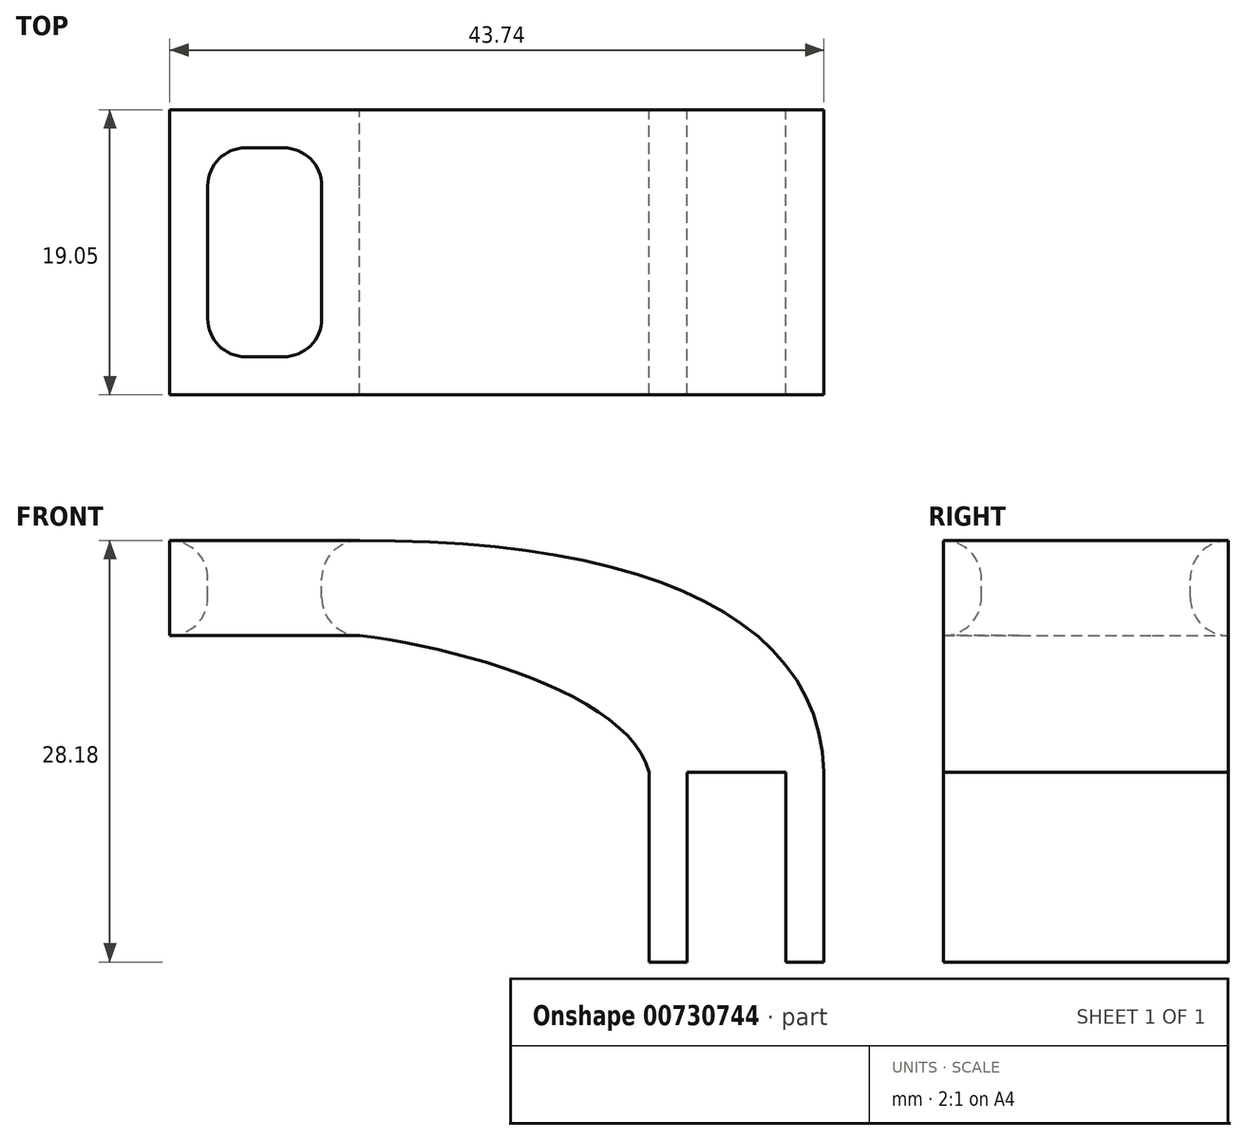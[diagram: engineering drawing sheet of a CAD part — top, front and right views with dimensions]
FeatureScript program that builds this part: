
annotation { "Feature Type Name" : "Feature", "Feature Type Description" : "" }
export const myFeature = defineFeature(function(context is Context, id is Id, definition is map)
    precondition{}
    {
        {
            var Q0;
            Q0=qCreatedBy(makeId("Front.planeOp"),FACE);
            var sketch = newSketch(context, id + "F0", { "sketchPlane" : qUnion([Q0])});
            skLineSegment(sketch, "E0.bottom", {"start": v(3.3, 6.35) * mm, "end": v(-3.3, 6.35) * mm});
            skLineSegment(sketch, "E0.left", {"start": v(3.3, 6.35) * mm, "end": v(3.3, -6.35) * mm});
            skLineSegment(sketch, "E0.right", {"start": v(-3.3, 6.35) * mm, "end": v(-3.3, -6.35) * mm});
            skPoint(sketch, "E0.middle", {"position": v(0, 0) * mm});
            skLineSegment(sketch, "E1.top", {"start": v(-3.3, -6.35) * mm, "end": v(-5.84, -6.35) * mm});
            skLineSegment(sketch, "E1.right", {"start": v(-5.84, 6.35) * mm, "end": v(-5.84, -6.35) * mm});
            skLineSegment(sketch, "E2.top", {"start": v(3.3, -6.35) * mm, "end": v(5.84, -6.35) * mm});
            skLineSegment(sketch, "E2.right", {"start": v(5.84, 6.35) * mm, "end": v(5.84, -6.35) * mm});
            skLineSegment(sketch, "E3.bottom", {"start": v(-25.2, 15.48) * mm, "end": v(-37.9, 15.48) * mm});
            skLineSegment(sketch, "E3.top", {"start": v(-25.2, 21.83) * mm, "end": v(-37.9, 21.83) * mm});
            skLineSegment(sketch, "E3.right", {"start": v(-37.9, 15.48) * mm, "end": v(-37.9, 21.83) * mm});
            skPoint(sketch, "E3.middle", {"position": v(-31.55, 18.65) * mm});
            skFitSpline(sketch, "E4", {"points": [v(-25.2, 21.83) * mm, v(5.84, 6.35) * mm], "startDerivative": vector(55.67, 0.15) * mm, "endDerivative": vector(0.93, -31.98) * mm});
            skFitSpline(sketch, "E5", {"points": [v(-25.2, 15.48) * mm, v(-5.84, 6.35) * mm], "startDerivative": vector(22.48, -2.8) * mm, "endDerivative": vector(3.82, -14.84) * mm});
            skSolve(sketch);
        }
        {
            var Q0;
            Q0=makeQuery(id+"F0.imprint","IMPRINT",FACE,{"disambiguationData":[TD([[makeQuery(id+"F0.imprint","IMPRINT",EDGE,{"derivedFrom":sQuery(id+"F0.wireOp",EDGE,"E0.bottom")}),-1.0]])]});
            extrude(context, id + "F1", {"entities" : qUnion([Q0]), "depth" : 19.05 * mm, "offsetDistance" : 25.4 * mm});
        }
        {
            var Q0;
            Q0=makeQuery(id+"F1.opExtrude","SWEPT_FACE",FACE,{"disambiguationData":[OSD([sQuery(id+"F0.wireOp",EDGE,"E3.top")])]});
            var sketch = newSketch(context, id + "F2", { "sketchPlane" : qUnion([Q0])});
            skLineSegment(sketch, "E6.0", {"start": v(-27.74, -2.54) * mm, "end": v(-35.36, -2.54) * mm});
            skLineSegment(sketch, "E6.1", {"start": v(-27.74, -16.51) * mm, "end": v(-27.74, -2.54) * mm});
            skLineSegment(sketch, "E6.2", {"start": v(-35.36, -16.51) * mm, "end": v(-27.74, -16.51) * mm});
            skLineSegment(sketch, "E6.3", {"start": v(-35.36, -2.54) * mm, "end": v(-35.36, -16.51) * mm});
            skSolve(sketch);
        }
        {
            var Q0;
            Q0=makeQuery(id+"F2.imprint","IMPRINT",FACE,{"disambiguationData":[TD([[makeQuery(id+"F2.imprint","IMPRINT",EDGE,{"derivedFrom":sQuery(id+"F2.wireOp",EDGE,"E6.0")}),1.0]])]});
            extrude(context, id + "F3", {"entities" : qUnion([Q0]), "operationType" : NewBodyOperationType.REMOVE, "oppositeDirection" : true, "depth" : 6.35 * mm, "offsetDistance" : 25.4 * mm});
        }
        {
            var Q0;
            Q0=makeQuery(id+"F3.boolean.opBoolean","COPY",EDGE,{"derivedFrom":makeQuery(id+"F3.opExtrude","SWEPT_EDGE",EDGE,{"disambiguationData":[OSD([sQuery(id+"F2.wireOp",EDGE,"E6.0"),sQuery(id+"F2.wireOp",EDGE,"E6.1")])]})});
            var Q1;
            Q1=makeQuery(id+"F3.boolean.opBoolean","COPY",EDGE,{"derivedFrom":makeQuery(id+"F3.opExtrude","SWEPT_EDGE",EDGE,{"disambiguationData":[OSD([sQuery(id+"F2.wireOp",EDGE,"E6.0"),sQuery(id+"F2.wireOp",EDGE,"E6.3")])]})});
            var Q2;
            Q2=makeQuery(id+"F3.boolean.opBoolean","COPY",EDGE,{"derivedFrom":makeQuery(id+"F3.opExtrude","SWEPT_EDGE",EDGE,{"disambiguationData":[OSD([sQuery(id+"F2.wireOp",EDGE,"E6.2"),sQuery(id+"F2.wireOp",EDGE,"E6.3")])]})});
            var Q3;
            Q3=makeQuery(id+"F3.boolean.opBoolean","COPY",EDGE,{"derivedFrom":makeQuery(id+"F3.opExtrude","SWEPT_EDGE",EDGE,{"disambiguationData":[OSD([sQuery(id+"F2.wireOp",EDGE,"E6.1"),sQuery(id+"F2.wireOp",EDGE,"E6.2")])]})});
            fillet(context, id + "F4", {"entities" : qUnion([Q0, Q1, Q2, Q3]), "radius" : 2.54 * mm, "tangentPropagation" : true, "allowEdgeOverflow" : false});
        }
        {
            var Q0;
            Q0=makeQuery(id+"F3.boolean.opBoolean","COPY",EDGE,{"derivedFrom":makeQuery(id+"F3.opExtrude","CAP_EDGE",EDGE,{"disambiguationData":[OSD([sQuery(id+"F2.wireOp",EDGE,"E6.3")])],"isStart":false})});
            var Q1;
            Q1=makeQuery(id+"F4.opFillet","BLEND_EDGE",EDGE,{"blendedFrom":[makeQuery(id+"F3.boolean.opBoolean","COPY",EDGE,{"derivedFrom":makeQuery(id+"F3.opExtrude","SWEPT_EDGE",EDGE,{"disambiguationData":[OSD([sQuery(id+"F2.wireOp",EDGE,"E6.2"),sQuery(id+"F2.wireOp",EDGE,"E6.3")])]})}),makeQuery(id+"F1.opExtrude","SWEPT_FACE",FACE,{"disambiguationData":[OSD([sQuery(id+"F0.wireOp",EDGE,"E3.bottom")])]})],"blendedInto":[makeQuery(id+"F1.opExtrude","SWEPT_FACE",FACE,{"disambiguationData":[OSD([sQuery(id+"F0.wireOp",EDGE,"E3.bottom")])]})]});
            var Q2;
            Q2=makeQuery(id+"F3.boolean.opBoolean","COPY",EDGE,{"derivedFrom":makeQuery(id+"F3.opExtrude","CAP_EDGE",EDGE,{"disambiguationData":[OSD([sQuery(id+"F2.wireOp",EDGE,"E6.2")])],"isStart":false})});
            var Q3;
            Q3=makeQuery(id+"F4.opFillet","BLEND_EDGE",EDGE,{"blendedFrom":[makeQuery(id+"F3.boolean.opBoolean","COPY",EDGE,{"derivedFrom":makeQuery(id+"F3.opExtrude","SWEPT_EDGE",EDGE,{"disambiguationData":[OSD([sQuery(id+"F2.wireOp",EDGE,"E6.1"),sQuery(id+"F2.wireOp",EDGE,"E6.2")])]})}),makeQuery(id+"F1.opExtrude","SWEPT_FACE",FACE,{"disambiguationData":[OSD([sQuery(id+"F0.wireOp",EDGE,"E3.bottom")])]})],"blendedInto":[makeQuery(id+"F1.opExtrude","SWEPT_FACE",FACE,{"disambiguationData":[OSD([sQuery(id+"F0.wireOp",EDGE,"E3.bottom")])]})]});
            var Q4;
            Q4=makeQuery(id+"F3.boolean.opBoolean","COPY",EDGE,{"derivedFrom":makeQuery(id+"F3.opExtrude","CAP_EDGE",EDGE,{"disambiguationData":[OSD([sQuery(id+"F2.wireOp",EDGE,"E6.1")])],"isStart":false})});
            var Q5;
            Q5=makeQuery(id+"F3.boolean.opBoolean","COPY",EDGE,{"derivedFrom":makeQuery(id+"F3.opExtrude","CAP_EDGE",EDGE,{"disambiguationData":[OSD([sQuery(id+"F2.wireOp",EDGE,"E6.0")])],"isStart":false})});
            var Q6;
            Q6=makeQuery(id+"F4.opFillet","BLEND_EDGE",EDGE,{"blendedFrom":[makeQuery(id+"F3.boolean.opBoolean","COPY",EDGE,{"derivedFrom":makeQuery(id+"F3.opExtrude","SWEPT_EDGE",EDGE,{"disambiguationData":[OSD([sQuery(id+"F2.wireOp",EDGE,"E6.0"),sQuery(id+"F2.wireOp",EDGE,"E6.3")])]})}),makeQuery(id+"F1.opExtrude","SWEPT_FACE",FACE,{"disambiguationData":[OSD([sQuery(id+"F0.wireOp",EDGE,"E3.bottom")])]})],"blendedInto":[makeQuery(id+"F1.opExtrude","SWEPT_FACE",FACE,{"disambiguationData":[OSD([sQuery(id+"F0.wireOp",EDGE,"E3.bottom")])]})]});
            var Q7;
            Q7=makeQuery(id+"F4.opFillet","BLEND_EDGE",EDGE,{"blendedFrom":[makeQuery(id+"F3.boolean.opBoolean","COPY",EDGE,{"derivedFrom":makeQuery(id+"F3.opExtrude","SWEPT_EDGE",EDGE,{"disambiguationData":[OSD([sQuery(id+"F2.wireOp",EDGE,"E6.0"),sQuery(id+"F2.wireOp",EDGE,"E6.1")])]})}),makeQuery(id+"F1.opExtrude","SWEPT_FACE",FACE,{"disambiguationData":[OSD([sQuery(id+"F0.wireOp",EDGE,"E3.bottom")])]})],"blendedInto":[makeQuery(id+"F1.opExtrude","SWEPT_FACE",FACE,{"disambiguationData":[OSD([sQuery(id+"F0.wireOp",EDGE,"E3.bottom")])]})]});
            fillet(context, id + "F5", {"entities" : qUnion([Q0, Q1, Q2, Q3, Q4, Q5, Q6, Q7]), "radius" : 2.54 * mm, "tangentPropagation" : true, "allowEdgeOverflow" : false});
        }
        {
            var Q0;
            Q0=makeQuery(id+"F3.boolean.opBoolean","COPY",EDGE,{"derivedFrom":makeQuery(id+"F3.opExtrude","CAP_EDGE",EDGE,{"disambiguationData":[OSD([sQuery(id+"F2.wireOp",EDGE,"E6.2")])],"isStart":true})});
            var Q1;
            Q1=makeQuery(id+"F4.opFillet","BLEND_EDGE",EDGE,{"blendedFrom":[makeQuery(id+"F3.boolean.opBoolean","COPY",EDGE,{"derivedFrom":makeQuery(id+"F3.opExtrude","SWEPT_EDGE",EDGE,{"disambiguationData":[OSD([sQuery(id+"F2.wireOp",EDGE,"E6.2"),sQuery(id+"F2.wireOp",EDGE,"E6.3")])]})}),makeQuery(id+"F1.opExtrude","SWEPT_FACE",FACE,{"disambiguationData":[OSD([sQuery(id+"F0.wireOp",EDGE,"E3.top")])]})],"blendedInto":[makeQuery(id+"F1.opExtrude","SWEPT_FACE",FACE,{"disambiguationData":[OSD([sQuery(id+"F0.wireOp",EDGE,"E3.top")])]})]});
            var Q2;
            Q2=makeQuery(id+"F4.opFillet","BLEND_EDGE",EDGE,{"blendedFrom":[makeQuery(id+"F3.boolean.opBoolean","COPY",EDGE,{"derivedFrom":makeQuery(id+"F3.opExtrude","SWEPT_EDGE",EDGE,{"disambiguationData":[OSD([sQuery(id+"F2.wireOp",EDGE,"E6.1"),sQuery(id+"F2.wireOp",EDGE,"E6.2")])]})}),makeQuery(id+"F1.opExtrude","SWEPT_FACE",FACE,{"disambiguationData":[OSD([sQuery(id+"F0.wireOp",EDGE,"E3.top")])]})],"blendedInto":[makeQuery(id+"F1.opExtrude","SWEPT_FACE",FACE,{"disambiguationData":[OSD([sQuery(id+"F0.wireOp",EDGE,"E3.top")])]})]});
            var Q3;
            Q3=makeQuery(id+"F3.boolean.opBoolean","COPY",EDGE,{"derivedFrom":makeQuery(id+"F3.opExtrude","CAP_EDGE",EDGE,{"disambiguationData":[OSD([sQuery(id+"F2.wireOp",EDGE,"E6.3")])],"isStart":true})});
            var Q4;
            Q4=makeQuery(id+"F3.boolean.opBoolean","COPY",EDGE,{"derivedFrom":makeQuery(id+"F3.opExtrude","CAP_EDGE",EDGE,{"disambiguationData":[OSD([sQuery(id+"F2.wireOp",EDGE,"E6.1")])],"isStart":true})});
            var Q5;
            Q5=makeQuery(id+"F4.opFillet","BLEND_EDGE",EDGE,{"blendedFrom":[makeQuery(id+"F3.boolean.opBoolean","COPY",EDGE,{"derivedFrom":makeQuery(id+"F3.opExtrude","SWEPT_EDGE",EDGE,{"disambiguationData":[OSD([sQuery(id+"F2.wireOp",EDGE,"E6.0"),sQuery(id+"F2.wireOp",EDGE,"E6.1")])]})}),makeQuery(id+"F1.opExtrude","SWEPT_FACE",FACE,{"disambiguationData":[OSD([sQuery(id+"F0.wireOp",EDGE,"E3.top")])]})],"blendedInto":[makeQuery(id+"F1.opExtrude","SWEPT_FACE",FACE,{"disambiguationData":[OSD([sQuery(id+"F0.wireOp",EDGE,"E3.top")])]})]});
            var Q6;
            Q6=makeQuery(id+"F3.boolean.opBoolean","COPY",EDGE,{"derivedFrom":makeQuery(id+"F3.opExtrude","CAP_EDGE",EDGE,{"disambiguationData":[OSD([sQuery(id+"F2.wireOp",EDGE,"E6.0")])],"isStart":true})});
            var Q7;
            Q7=makeQuery(id+"F4.opFillet","BLEND_EDGE",EDGE,{"blendedFrom":[makeQuery(id+"F3.boolean.opBoolean","COPY",EDGE,{"derivedFrom":makeQuery(id+"F3.opExtrude","SWEPT_EDGE",EDGE,{"disambiguationData":[OSD([sQuery(id+"F2.wireOp",EDGE,"E6.0"),sQuery(id+"F2.wireOp",EDGE,"E6.3")])]})}),makeQuery(id+"F1.opExtrude","SWEPT_FACE",FACE,{"disambiguationData":[OSD([sQuery(id+"F0.wireOp",EDGE,"E3.top")])]})],"blendedInto":[makeQuery(id+"F1.opExtrude","SWEPT_FACE",FACE,{"disambiguationData":[OSD([sQuery(id+"F0.wireOp",EDGE,"E3.top")])]})]});
            fillet(context, id + "F6", {"entities" : qUnion([Q0, Q1, Q2, Q3, Q4, Q5, Q6, Q7]), "radius" : 2.54 * mm, "tangentPropagation" : true, "allowEdgeOverflow" : false});
        }
    });
